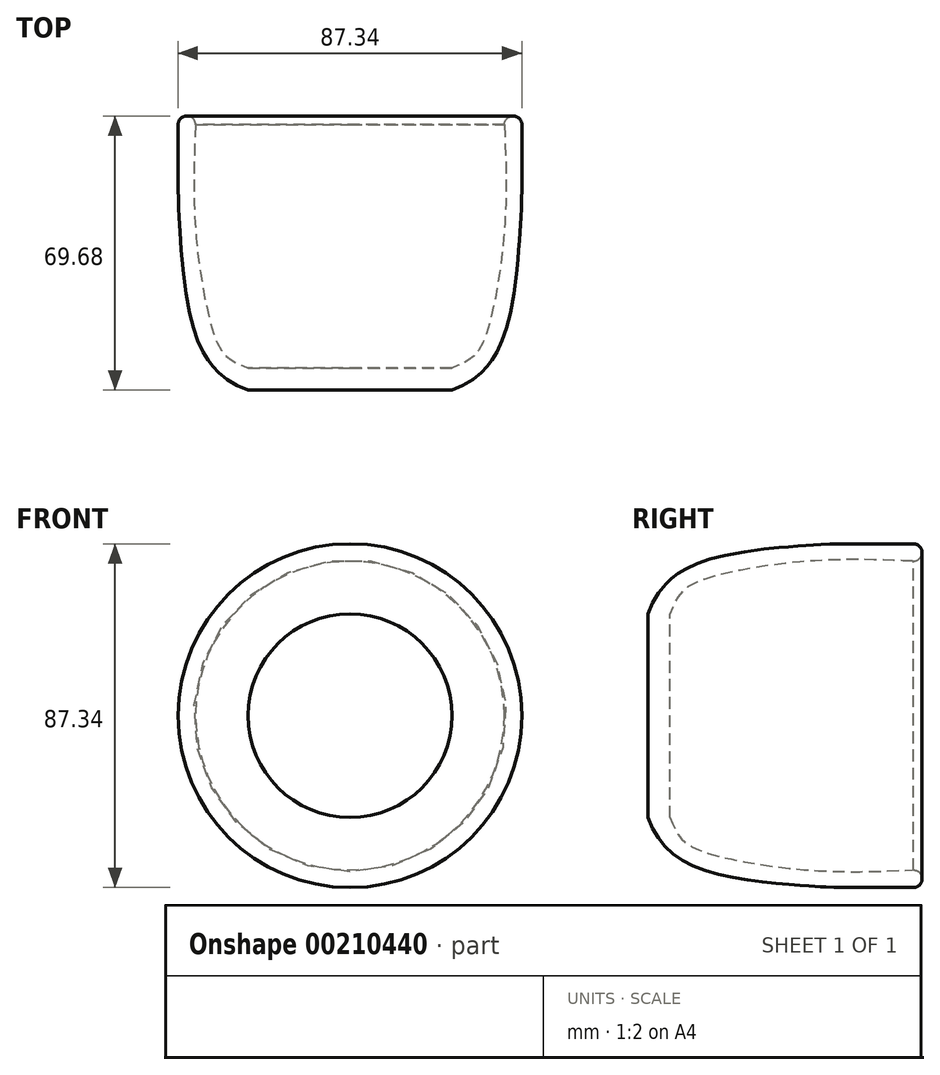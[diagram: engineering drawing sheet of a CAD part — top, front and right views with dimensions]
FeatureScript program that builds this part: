
annotation { "Feature Type Name" : "Feature", "Feature Type Description" : "" }
export const myFeature = defineFeature(function(context is Context, id is Id, definition is map)
    precondition{}
    {
        {
            var Q0;
            Q0=qCreatedBy(makeId("Top.planeOp"),FACE);
            var sketch = newSketch(context, id + "F0", { "sketchPlane" : qUnion([Q0])});
            skLineSegment(sketch, "E0", {"start": v(0, 0) * mm, "end": v(0, 5.67) * mm});
            skLineSegment(sketch, "E1", {"start": v(0, 0) * mm, "end": v(-25.9, 0) * mm});
            skFitSpline(sketch, "E2", {"points": [v(-25.9, 0) * mm, v(-39.23, 14.11) * mm, v(-43.23, 40.78) * mm, v(-43.67, 67.45) * mm], "startDerivative": vector(-66.76, 24.94) * mm, "endDerivative": vector(0, 203.74) * mm});
            skLineSegment(sketch, "E3", {"start": v(0, 5.67) * mm, "end": v(-25.9, 5.67) * mm});
            skFitSpline(sketch, "E4", {"points": [v(-25.9, 5.67) * mm, v(-30.78, 8.11) * mm, v(-34.56, 14.11) * mm, v(-39.23, 40.78) * mm, v(-39.23, 67.45) * mm], "startDerivative": vector(-34.47, 13.5) * mm, "endDerivative": vector(3.26, 75.83) * mm});
            skArc(sketch, "E5", {"start": v(-39.24, 67.26) * mm, "mid": v(-41.35, 69.67) * mm, "end": v(-43.67, 67.45) * mm});
            skSolve(sketch);
        }
        {
            var Q0;
            Q0=makeQuery(id+"F0.imprint","IMPRINT",FACE,{"disambiguationData":[TD([[makeQuery(id+"F0.imprint","IMPRINT",EDGE,{"derivedFrom":sQuery(id+"F0.wireOp",EDGE,"E0")}),1.0]])]});
            var Q1;
            Q1=sQuery(id+"F0.wireOp",EDGE,"E0");
            revolve(context, id + "F1", {"surfaceOperationType" : NewSurfaceOperationType.NEW, "entities" : qUnion([Q0]), "axis" : qUnion([Q1]), "revolveType" : RevolveType.FULL});
        }
    });
